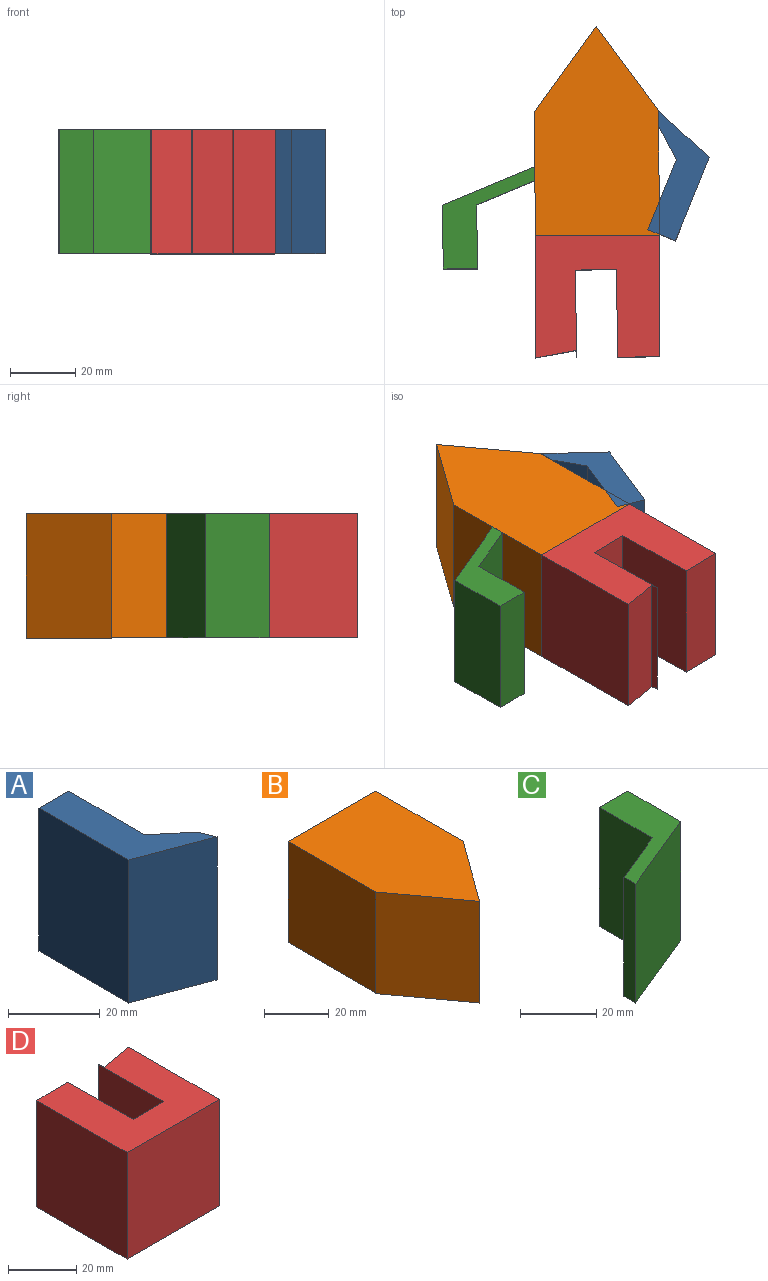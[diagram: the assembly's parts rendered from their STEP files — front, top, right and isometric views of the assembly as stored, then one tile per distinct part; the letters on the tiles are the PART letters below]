
ASSEMBLY  parts=4 mates=3
PART A: 8 faces, bbox 19.7x35x38.1 mm
  f0: plane 38.1x8.84mm, normal (0.64,0.77,0), area 438.3mm2, adj f1,f5,f6,f7
  f1: plane 38.1x23.36mm, normal (1,0,0), area 890mm2, adj f0,f2,f6,f7
  f2: plane 38.1x9.13mm, normal (0,1,0), area 347.8mm2, adj f1,f3,f6,f7
  f3: plane 38.1x27.65mm, normal (-1,0,0), area 1053.6mm2, adj f2,f4,f6,f7
  f4: plane 38.1x19.75mm, normal (-0.35,-0.94,0), area 803.1mm2, adj f3,f5,f6,f7
  f5: plane 38.1x4.31mm, normal (0.92,0.38,0), area 177.6mm2, adj f0,f4,f6,f7
  f6: plane 35.03x19.75mm, normal (0,0,-1), area 321.4mm2, adj f0,f1,f2,f3,f4,f5
  f7: plane 35.03x19.75mm, normal (0,0,1), area 321.4mm2, adj f0,f1,f2,f3,f4,f5
PART B: 9 faces, bbox 38.1x64.3x38.4 mm
  f0: plane 38.1x38.1mm, normal (0,1,0), area 1451.6mm2, adj f1,f2,f3,f4
  f1: plane 38.1x38.1mm, normal (-1,0,0), area 1451.6mm2, adj f0,f3,f4,f6
  f2: plane 38.1x38.1mm, normal (1,0,0), area 1451.6mm2, adj f0,f3,f4,f7
  f3: plane 64.29x38.1mm, normal (0,0,1), area 1950.5mm2, adj f0,f1,f2,f6,f7
  f4: plane 38.1x38.1mm, normal (0,0,-1), area 1451.6mm2, adj f0,f1,f2,f5
  f5: plane 38.1x0.25mm, normal (0,1,0), area 9.7mm2, adj f4,f6,f7,f8
  f6: plane 38.35x26.19mm, normal (-0.81,-0.59,0), area 1242.1mm2, adj f1,f3,f5,f7,f8
  f7: plane 38.35x26.19mm, normal (0.81,-0.59,0), area 1242.1mm2, adj f2,f3,f5,f6,f8
  f8: plane 38.1x26.19mm, normal (0,0,-1), area 498.9mm2, adj f5,f6,f7
PART C: 8 faces, bbox 28.3x31.3x38.1 mm
  f0: plane 38.1x19.6mm, normal (-1,0,0), area 746.8mm2, adj f1,f5,f6,f7
  f1: plane 38.1x17.87mm, normal (-0.38,0.92,0), area 736.2mm2, adj f0,f2,f6,f7
  f2: plane 38.1x4.31mm, normal (-1,0,0), area 164.2mm2, adj f1,f3,f6,f7
  f3: plane 38.1x28.34mm, normal (0.38,-0.92,0), area 1167.6mm2, adj f2,f4,f6,f7
  f4: plane 38.1x19.6mm, normal (1,0,0), area 746.8mm2, adj f3,f5,f6,f7
  f5: plane 38.1x10.47mm, normal (0,1,0), area 398.9mm2, adj f0,f4,f6,f7
  f6: plane 31.27x28.34mm, normal (0,0,-1), area 304.8mm2, adj f0,f1,f2,f3,f4,f5
  f7: plane 31.27x28.34mm, normal (0,0,1), area 304.8mm2, adj f0,f1,f2,f3,f4,f5
PART D: 11 faces, bbox 38.1x37.5x38.1 mm
  f0: plane 38.1x12.92mm, normal (-0.01,1,0), area 492.2mm2, adj f1,f8,f9,f10
  f1: plane 38.1x37.29mm, normal (-1,0,0), area 1420.6mm2, adj f0,f2,f9,f10
  f2: plane 38.1x38.1mm, normal (0,-1,0), area 1451.6mm2, adj f1,f3,f9,f10
  f3: plane 38.1x37.47mm, normal (1,0,0), area 1427.5mm2, adj f2,f4,f9,f10
  f4: plane 38.1x12.2mm, normal (-0.17,0.98,0), area 472.1mm2, adj f3,f5,f9,f10
  f5: plane 38.1x2.15mm, normal (0.98,0.17,0), area 83.1mm2, adj f4,f6,f9,f10
  f6: plane 38.1x26.85mm, normal (-1,-0.01,0), area 1023mm2, adj f5,f7,f9,f10
  f7: plane 38.1x12.6mm, normal (-0.01,1,0), area 480mm2, adj f6,f8,f9,f10
  f8: plane 38.1x27.03mm, normal (1,0.01,0), area 1029.8mm2, adj f0,f7,f9,f10
  f9: plane 38.1x37.47mm, normal (0,0,-1), area 1073.4mm2, adj f0,f1,f2,f3,f4,f5,f6,f7
  f10: plane 38.1x37.47mm, normal (0,0,1), area 1073.4mm2, adj f0,f1,f2,f3,f4,f5,f6,f7
PLACE A rot(axis=(0,0,1),157.9deg) t=(-85.15,66.08,49.78)mm
PLACE B rot(axis=(0,0,-1),179.7deg) t=(-79.28,57.43,49.78)mm
PLACE C rot(axis=(0,0,-1),179.7deg) t=(-79.19,40.53,49.78)mm
PLACE D rot(axis=(0,0,-1),179.7deg) t=(-79.28,57.43,49.78)mm
MATE fastened D.f2 <-> B.f0  axis (-0.01,1,0) through (-79.18,38.38,49.78)mm
MATE fastened C.f2 <-> B.f2  axis (1,0.01,0) through (-98.33,57.32,68.83)mm
MATE fastened A.f5 <-> B.f1  axis (-1,-0.01,0) through (-60.34,76.58,68.83)mm
